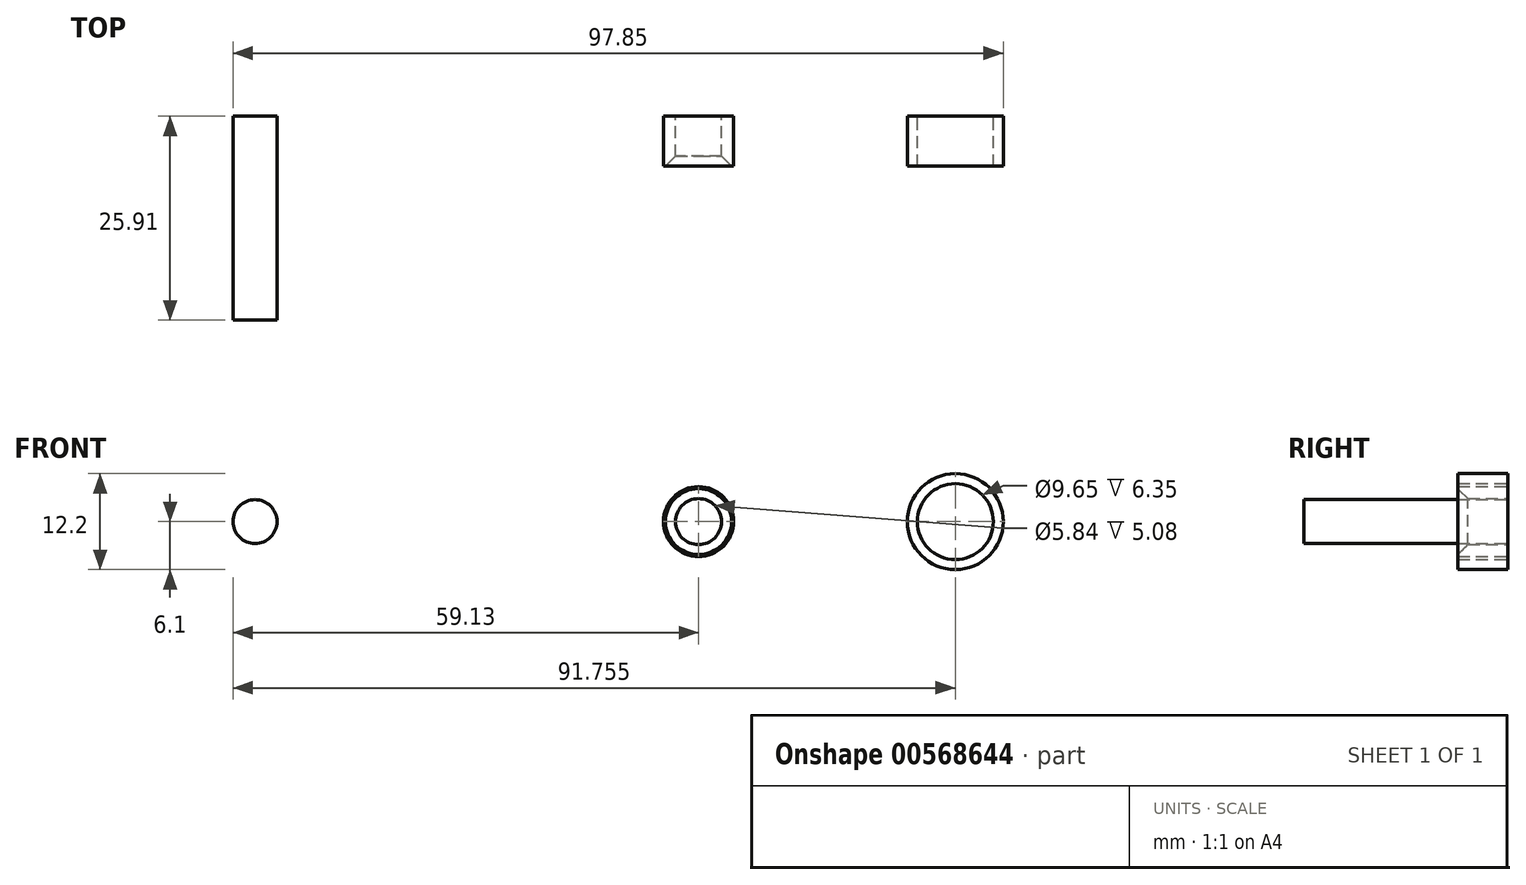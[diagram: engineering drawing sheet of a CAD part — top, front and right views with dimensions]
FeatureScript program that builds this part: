
annotation { "Feature Type Name" : "Feature", "Feature Type Description" : "" }
export const myFeature = defineFeature(function(context is Context, id is Id, definition is map)
    precondition{}
    {
        {
            var Q0;
            Q0=qCreatedBy(makeId("Front.planeOp"),FACE);
            var sketch = newSketch(context, id + "F0", { "sketchPlane" : qUnion([Q0])});
            skCircle(sketch, "E0", {"center": v(0, 0) * mm, "radius": 2.92 * mm});
            skCircle(sketch, "E1", {"center": v(0, 0) * mm, "radius": 4.45 * mm});
            skSolve(sketch);
        }
        {
            var Q0;
            Q0 = qSketchRegion(id + "F0", true);
            extrude(context, id + "F1", {"entities" : qUnion([Q0]), "depth" : 6.35 * mm, "offsetDistance" : 25.4 * mm});
        }
        {
            var Q0;
            Q0=qCreatedBy(makeId("Front.planeOp"),FACE);
            var sketch = newSketch(context, id + "F2", { "sketchPlane" : qUnion([Q0])});
            skCircle(sketch, "E2", {"center": v(32.63, 0) * mm, "radius": 4.83 * mm});
            skCircle(sketch, "E3", {"center": v(32.63, 0) * mm, "radius": 6.1 * mm});
            skSolve(sketch);
        }
        {
            var Q0;
            Q0 = qSketchRegion(id + "F2", true);
            extrude(context, id + "F3", {"entities" : qUnion([Q0]), "depth" : 6.35 * mm, "offsetDistance" : 25.4 * mm});
        }
        {
            var Q0;
            Q0=makeQuery(id+"F1.opExtrude","CAP_EDGE",EDGE,{"disambiguationData":[OSD([sQuery(id+"F0.wireOp",EDGE,"E0")])],"isStart":false});
            chamfer(context, id + "F4", {"entities" : qUnion([Q0]), "width" : 1.27 * mm, "tangentPropagation" : true});
        }
        {
            var Q0;
            Q0=qCreatedBy(makeId("Front.planeOp"),FACE);
            var sketch = newSketch(context, id + "F5", { "sketchPlane" : qUnion([Q0])});
            skCircle(sketch, "E4", {"center": v(-56.34, 0) * mm, "radius": 2.8 * mm});
            skSolve(sketch);
        }
        {
            var Q0;
            Q0=makeQuery(id+"F5.imprint","IMPRINT",FACE,{"disambiguationData":[TD([[makeQuery(id+"F5.imprint","IMPRINT",EDGE,{"derivedFrom":sQuery(id+"F5.wireOp",EDGE,"E4")}),1.0]])]});
            extrude(context, id + "F6", {"entities" : qUnion([Q0]), "depth" : 25.9 * mm, "offsetDistance" : 25.4 * mm});
        }
    });
